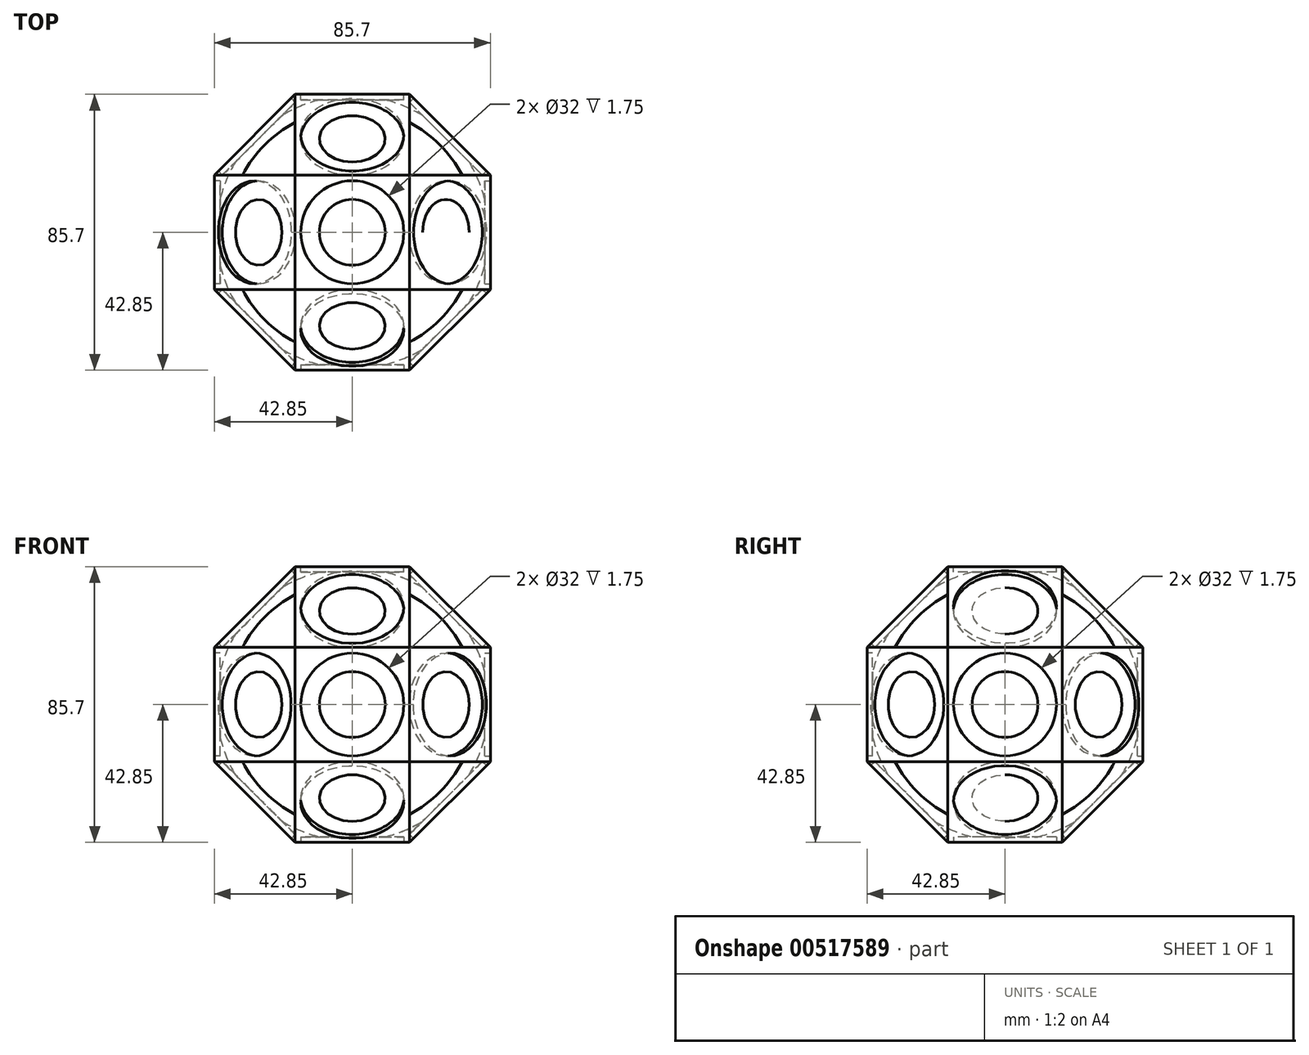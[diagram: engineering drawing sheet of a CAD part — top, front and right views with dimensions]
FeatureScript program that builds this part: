
annotation { "Feature Type Name" : "Feature", "Feature Type Description" : "" }
export const myFeature = defineFeature(function(context is Context, id is Id, definition is map)
    precondition{}
    {
        {
            assignVariable(context, id + "F0", {"name" : "Connector", "anyValue" : 16});
        }
        {
            assignVariable(context, id + "F1", {"name" : "Margin", "anyValue" : .25});
        }
        {
            assignVariable(context, id + "F2", {"name" : "Thickness", "anyValue" : .5});
        }
        {
            assignVariable(context, id + "F3", {"name" : "Radius", "anyValue" : ((getVariable(context, 'Connector') + getVariable(context, 'Margin') + getVariable(context, 'Thickness') * 3)) * mm});
        }
        {
            var Q0;
            Q0=qCreatedBy(makeId("Front.planeOp"),FACE);
            var sketch = newSketch(context, id + "F4", { "sketchPlane" : qUnion([Q0])});
            skLineSegment(sketch, "E0", {"start": v(0, 0) * mm, "end": v(0, 17.75) * mm});
            skLineSegment(sketch, "E1", {"start": v(0, 17.75) * mm, "end": v(42.85, 17.75) * mm});
            skLineSegment(sketch, "E2", {"start": v(42.85, 17.75) * mm, "end": v(42.85, 0) * mm});
            skLineSegment(sketch, "E3", {"start": v(42.85, 0) * mm, "end": v(42.85, -17.75) * mm});
            skLineSegment(sketch, "E4", {"start": v(42.85, -17.75) * mm, "end": v(0, -17.75) * mm});
            skLineSegment(sketch, "E5", {"start": v(0, -17.75) * mm, "end": v(0, 0) * mm});
            skLineSegment(sketch, "E6", {"start": v(0, 0) * mm, "end": v(17.75, 0) * mm, "construction": true});
            skLineSegment(sketch, "E7", {"start": v(17.75, 0) * mm, "end": v(17.75, -42.85) * mm, "construction": true});
            skLineSegment(sketch, "E8", {"start": v(17.75, -42.85) * mm, "end": v(30.3, -30.3) * mm, "construction": true});
            skLineSegment(sketch, "E9", {"start": v(30.3, -30.3) * mm, "end": v(42.85, -17.75) * mm, "construction": true});
            skLineSegment(sketch, "E10", {"start": v(0, 17.75) * mm, "end": v(0, 42.35) * mm});
            skLineSegment(sketch, "E11", {"start": v(0, 42.35) * mm, "end": v(0, 42.85) * mm});
            skLineSegment(sketch, "E12", {"start": v(0, 42.85) * mm, "end": v(17.75, 42.85) * mm, "construction": true});
            skLineSegment(sketch, "E13", {"start": v(17.75, 42.85) * mm, "end": v(17.75, 0) * mm, "construction": true});
            skArc(sketch, "E14", {"start": v(0, 42.35) * mm, "mid": v(-42.35, 0) * mm, "end": v(0, -42.35) * mm});
            skLineSegment(sketch, "E15", {"start": v(0, -17.75) * mm, "end": v(0, -42.35) * mm});
            skSolve(sketch);
        }
        {
            var Q0;
            Q0=makeQuery(id+"F4.imprint","IMPRINT",FACE,{"disambiguationData":[TD([[makeQuery(id+"F4.imprint","IMPRINT",EDGE,{"derivedFrom":sQuery(id+"F4.wireOp",EDGE,"E0")}),-1.0]])]});
            extrude(context, id + "F5", {"entities" : qUnion([Q0]), "depth" : getVariable(context, 'Radius'), "offsetDistance" : 25 * mm, "hasSecondDirection" : true, "secondDirectionOppositeDirection" : true, "secondDirectionDepth" : getVariable(context, 'Radius')});
        }
        {
            var Q0;
            Q0=makeQuery(id+"F5.opExtrude","SWEPT_FACE",FACE,{"disambiguationData":[OSD([sQuery(id+"F4.wireOp",EDGE,"E2"),sQuery(id+"F4.wireOp",EDGE,"E3")])]});
            var sketch = newSketch(context, id + "F6", { "sketchPlane" : qUnion([Q0])});
            skCircle(sketch, "E16", {"center": v(0, 0) * mm, "radius": 16 * mm});
            skLineSegment(sketch, "E17", {"start": v(0, 0) * mm, "end": v(0, 16) * mm, "construction": true});
            skSolve(sketch);
        }
        {
            var Q0;
            Q0=makeQuery(id+"F6.imprint","IMPRINT",FACE,{"disambiguationData":[TD([[makeQuery(id+"F6.imprint","IMPRINT",EDGE,{"derivedFrom":sQuery(id+"F6.wireOp",EDGE,"E16")}),1.0]])]});
            extrude(context, id + "F7", {"entities" : qUnion([Q0]), "operationType" : NewBodyOperationType.REMOVE, "oppositeDirection" : true, "depth" : (getVariable(context, 'Thickness') * 3 + getVariable(context, 'Margin')) * mm, "offsetDistance" : 25 * mm});
        }
        {
            var Q0;
            Q0=makeQuery(id+"F5.opExtrude","SWEPT_BODY",BODY,{"disambiguationData":[OSD([sQuery(id+"F4.wireOp",EDGE,"E0"),sQuery(id+"F4.wireOp",EDGE,"E1"),sQuery(id+"F4.wireOp",EDGE,"E2"),sQuery(id+"F4.wireOp",EDGE,"E3"),sQuery(id+"F4.wireOp",EDGE,"E4"),sQuery(id+"F4.wireOp",EDGE,"E5")])]});
            var Q1;
            Q1=sQuery(id+"F4.wireOp",EDGE,"E0");
            circularPattern(context, id + "F8", {"operationType" : NewBodyOperationType.ADD, "entities" : qUnion([Q0]), "axis" : qUnion([Q1]), "angle" : 360 * degree, "instanceCount" : 8, "equalSpace" : true});
        }
        {
            var Q0;
            Q0=makeQuery(id+"F5.opExtrude","SWEPT_BODY",BODY,{"disambiguationData":[OSD([sQuery(id+"F4.wireOp",EDGE,"E0"),sQuery(id+"F4.wireOp",EDGE,"E1"),sQuery(id+"F4.wireOp",EDGE,"E2"),sQuery(id+"F4.wireOp",EDGE,"E3"),sQuery(id+"F4.wireOp",EDGE,"E4"),sQuery(id+"F4.wireOp",EDGE,"E5")])]});
            var Q1;
            Q1=sQuery(id+"F4.wireOp",EDGE,"E6");
            circularPattern(context, id + "F9", {"operationType" : NewBodyOperationType.ADD, "entities" : qUnion([Q0]), "axis" : qUnion([Q1]), "angle" : 90 * degree, "instanceCount" : 2, "equalSpace" : true});
        }
        {
            var Q0;
            Q0=makeQuery(id+"F5.opExtrude","SWEPT_BODY",BODY,{"disambiguationData":[OSD([sQuery(id+"F4.wireOp",EDGE,"E0"),sQuery(id+"F4.wireOp",EDGE,"E1"),sQuery(id+"F4.wireOp",EDGE,"E2"),sQuery(id+"F4.wireOp",EDGE,"E3"),sQuery(id+"F4.wireOp",EDGE,"E4"),sQuery(id+"F4.wireOp",EDGE,"E5")])]});
            var Q1;
            Q1=sQuery(id+"F4.wireOp",EDGE,"E0");
            circularPattern(context, id + "F10", {"operationType" : NewBodyOperationType.ADD, "entities" : qUnion([Q0]), "axis" : qUnion([Q1]), "angle" : 90 * degree, "instanceCount" : 2, "equalSpace" : true});
        }
        {
            var Q0;
            Q0=makeQuery(id+"F4.imprint","IMPRINT",FACE,{"disambiguationData":[TD([[makeQuery(id+"F4.imprint","IMPRINT",EDGE,{"derivedFrom":sQuery(id+"F4.wireOp",EDGE,"E0")}),1.0]])]});
            var Q1;
            Q1=sQuery(id+"F4.wireOp",EDGE,"E15");
            revolve(context, id + "F11", {"entities" : qUnion([Q0]), "axis" : qUnion([Q1]), "revolveType" : RevolveType.FULL});
        }
        {
            var Q0;
            Q0=makeQuery(id+"F11.opRevolve","SWEPT_BODY",BODY,{"disambiguationData":[OSD([sQuery(id+"F4.wireOp",EDGE,"E0"),sQuery(id+"F4.wireOp",EDGE,"E5"),sQuery(id+"F4.wireOp",EDGE,"E10"),sQuery(id+"F4.wireOp",EDGE,"E14"),sQuery(id+"F4.wireOp",EDGE,"E15")])]});
            var Q1;
            Q1=makeQuery(id+"F5.opExtrude","SWEPT_BODY",BODY,{"disambiguationData":[OSD([sQuery(id+"F4.wireOp",EDGE,"E0"),sQuery(id+"F4.wireOp",EDGE,"E1"),sQuery(id+"F4.wireOp",EDGE,"E2"),sQuery(id+"F4.wireOp",EDGE,"E3"),sQuery(id+"F4.wireOp",EDGE,"E4"),sQuery(id+"F4.wireOp",EDGE,"E5")])]});
            booleanBodies(context, id + "F12", {"operationType" : BooleanOperationType.SUBTRACTION, "tools" : qUnion([Q0]), "targets" : qUnion([Q1])});
        }
    });
